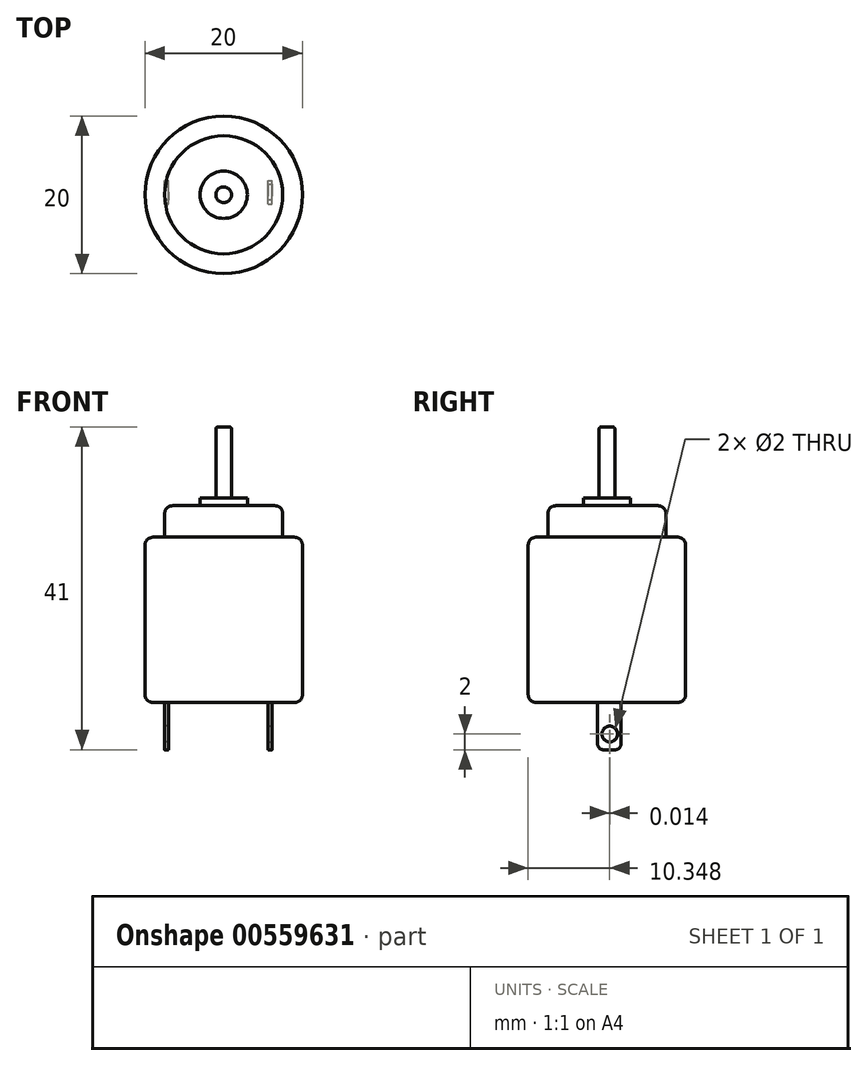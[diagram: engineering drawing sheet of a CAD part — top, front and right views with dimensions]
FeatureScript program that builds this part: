
annotation { "Feature Type Name" : "Feature", "Feature Type Description" : "" }
export const myFeature = defineFeature(function(context is Context, id is Id, definition is map)
    precondition{}
    {
        {
            var Q0;
            Q0=qCreatedBy(makeId("Top.planeOp"),FACE);
            var sketch = newSketch(context, id + "F0", { "sketchPlane" : qUnion([Q0])});
            skCircle(sketch, "E0", {"center": v(0, 0) * mm, "radius": 10 * mm});
            skSolve(sketch);
        }
        {
            var Q0;
            Q0 = qSketchRegion(id + "F0", true);
            extrude(context, id + "F1", {"entities" : qUnion([Q0]), "depth" : 21 * mm, "offsetDistance" : 25 * mm});
        }
        {
            var Q0;
            Q0=makeQuery(id+"F1.opExtrude","CAP_FACE",FACE,{"disambiguationData":[OSD([sQuery(id+"F0.wireOp",EDGE,"E0")])],"isStart":false});
            var sketch = newSketch(context, id + "F2", { "sketchPlane" : qUnion([Q0])});
            skCircle(sketch, "E1", {"center": v(0, 0) * mm, "radius": 7.5 * mm});
            skSolve(sketch);
        }
        {
            var Q0;
            Q0 = qSketchRegion(id + "F2", true);
            extrude(context, id + "F3", {"entities" : qUnion([Q0]), "operationType" : NewBodyOperationType.ADD, "depth" : 4 * mm, "offsetDistance" : 25 * mm});
        }
        {
            var Q0;
            Q0=makeQuery(id+"F3.opExtrude","CAP_FACE",FACE,{"disambiguationData":[OSD([sQuery(id+"F2.wireOp",EDGE,"E1")])],"isStart":false});
            var sketch = newSketch(context, id + "F4", { "sketchPlane" : qUnion([Q0])});
            skCircle(sketch, "E2", {"center": v(0, 0) * mm, "radius": 3 * mm});
            skSolve(sketch);
        }
        {
            var Q0;
            Q0 = qSketchRegion(id + "F4", true);
            extrude(context, id + "F5", {"entities" : qUnion([Q0]), "operationType" : NewBodyOperationType.ADD, "depth" : 1 * mm, "offsetDistance" : 25 * mm});
        }
        {
            var Q0;
            Q0=makeQuery(id+"F1.opExtrude","CAP_EDGE",EDGE,{"disambiguationData":[OSD([sQuery(id+"F0.wireOp",EDGE,"E0")])],"isStart":true});
            fillet(context, id + "F6", {"entities" : qUnion([Q0]), "radius" : 1 * mm, "tangentPropagation" : true, "allowEdgeOverflow" : false});
        }
        {
            var Q0;
            Q0=makeQuery(id+"F1.opExtrude","CAP_EDGE",EDGE,{"disambiguationData":[OSD([sQuery(id+"F0.wireOp",EDGE,"E0")])],"isStart":false});
            fillet(context, id + "F7", {"entities" : qUnion([Q0]), "radius" : 1 * mm, "tangentPropagation" : true, "allowEdgeOverflow" : false});
        }
        {
            var Q0;
            Q0=makeQuery(id+"F3.opExtrude","CAP_EDGE",EDGE,{"disambiguationData":[OSD([sQuery(id+"F2.wireOp",EDGE,"E1")])],"isStart":false});
            fillet(context, id + "F8", {"entities" : qUnion([Q0]), "radius" : 1 * mm, "tangentPropagation" : true, "allowEdgeOverflow" : false});
        }
        {
            var Q0;
            Q0=makeQuery(id+"F5.opExtrude","CAP_FACE",FACE,{"disambiguationData":[OSD([sQuery(id+"F4.wireOp",EDGE,"E2")])],"isStart":false});
            var sketch = newSketch(context, id + "F9", { "sketchPlane" : qUnion([Q0])});
            skCircle(sketch, "E3", {"center": v(0, 0) * mm, "radius": 1 * mm});
            skSolve(sketch);
        }
        {
            var Q0;
            Q0 = qSketchRegion(id + "F9", true);
            extrude(context, id + "F10", {"entities" : qUnion([Q0]), "operationType" : NewBodyOperationType.ADD, "depth" : 9 * mm, "offsetDistance" : 25 * mm});
        }
        {
            var Q0;
            Q0=makeQuery(id+"F10.opExtrude","CAP_EDGE",EDGE,{"disambiguationData":[OSD([sQuery(id+"F9.wireOp",EDGE,"E3")])],"isStart":false});
            fillet(context, id + "F11", {"entities" : qUnion([Q0]), "radius" : .25 * mm, "tangentPropagation" : true, "allowEdgeOverflow" : false});
        }
        {
            var Q0;
            Q0=makeQuery(id+"F1.opExtrude","CAP_FACE",FACE,{"disambiguationData":[OSD([sQuery(id+"F0.wireOp",EDGE,"E0")])],"isStart":true});
            var sketch = newSketch(context, id + "F12", { "sketchPlane" : qUnion([Q0])});
            skLineSegment(sketch, "E4.bottom", {"start": v(-7.52, 1.2) * mm, "end": v(-7.02, 1.2) * mm});
            skLineSegment(sketch, "E4.top", {"start": v(-7.52, -1.8) * mm, "end": v(-7.02, -1.8) * mm});
            skLineSegment(sketch, "E4.left", {"start": v(-7.52, 1.2) * mm, "end": v(-7.52, -1.8) * mm});
            skLineSegment(sketch, "E4.right", {"start": v(-7.02, 1.2) * mm, "end": v(-7.02, -1.8) * mm});
            skLineSegment(sketch, "E5.bottom", {"start": v(5.64, 1.2) * mm, "end": v(6.14, 1.2) * mm});
            skLineSegment(sketch, "E5.top", {"start": v(5.64, -1.8) * mm, "end": v(6.14, -1.8) * mm});
            skLineSegment(sketch, "E5.left", {"start": v(5.64, 1.2) * mm, "end": v(5.64, -1.8) * mm});
            skLineSegment(sketch, "E5.right", {"start": v(6.14, 1.2) * mm, "end": v(6.14, -1.8) * mm});
            skPoint(sketch, "E6.endSnap0", {"position": v(4.5, 0) * mm});
            skPoint(sketch, "E7.orphan", {"position": v(-9, 0) * mm});
            skPoint(sketch, "E8.orphan", {"position": v(0, 0) * mm});
            skPoint(sketch, "E9.end.orphan", {"position": v(9, 0) * mm});
            skSolve(sketch);
        }
        {
            var Q0;
            Q0 = qSketchRegion(id + "F12", true);
            extrude(context, id + "F13", {"entities" : qUnion([Q0]), "operationType" : NewBodyOperationType.ADD, "depth" : 6 * mm, "offsetDistance" : 25 * mm});
        }
        {
            var Q0;
            Q0=makeQuery(id+"F13.opExtrude","SWEPT_FACE",FACE,{"disambiguationData":[OSD([sQuery(id+"F12.wireOp",EDGE,"E4.left")])]});
            var sketch = newSketch(context, id + "F14", { "sketchPlane" : qUnion([Q0])});
            skCircle(sketch, "E10", {"center": v(-0.35, -4) * mm, "radius": 1 * mm});
            skSolve(sketch);
        }
        {
            var Q0;
            Q0 = qSketchRegion(id + "F14", true);
            extrude(context, id + "F15", {"entities" : qUnion([Q0]), "operationType" : NewBodyOperationType.REMOVE, "oppositeDirection" : true, "depth" : 3 * mm, "offsetDistance" : 25 * mm});
        }
        {
            var Q0;
            Q0=makeQuery(id+"F13.opExtrude","SWEPT_FACE",FACE,{"disambiguationData":[OSD([sQuery(id+"F12.wireOp",EDGE,"E5.right")])]});
            var sketch = newSketch(context, id + "F16", { "sketchPlane" : qUnion([Q0])});
            skCircle(sketch, "E11", {"center": v(0.36, -4) * mm, "radius": 1 * mm});
            skSolve(sketch);
        }
        {
            var Q0;
            Q0 = qSketchRegion(id + "F16", true);
            extrude(context, id + "F17", {"entities" : qUnion([Q0]), "operationType" : NewBodyOperationType.REMOVE, "oppositeDirection" : true, "depth" : 3 * mm, "offsetDistance" : 25 * mm});
        }
        {
            var Q0;
            Q0=makeQuery(id+"F13.opExtrude","CAP_EDGE",EDGE,{"disambiguationData":[OSD([sQuery(id+"F12.wireOp",EDGE,"E4.bottom")])],"isStart":false});
            var Q1;
            Q1=makeQuery(id+"F13.opExtrude","CAP_EDGE",EDGE,{"disambiguationData":[OSD([sQuery(id+"F12.wireOp",EDGE,"E4.top")])],"isStart":false});
            fillet(context, id + "F18", {"entities" : qUnion([Q0, Q1]), "radius" : .75 * mm, "tangentPropagation" : true, "allowEdgeOverflow" : false});
        }
        {
            var Q0;
            Q0=makeQuery(id+"F13.opExtrude","CAP_EDGE",EDGE,{"disambiguationData":[OSD([sQuery(id+"F12.wireOp",EDGE,"E5.bottom")])],"isStart":false});
            var Q1;
            Q1=makeQuery(id+"F13.opExtrude","CAP_EDGE",EDGE,{"disambiguationData":[OSD([sQuery(id+"F12.wireOp",EDGE,"E5.top")])],"isStart":false});
            fillet(context, id + "F19", {"entities" : qUnion([Q0, Q1]), "radius" : .75 * mm, "tangentPropagation" : true, "allowEdgeOverflow" : false});
        }
    });
